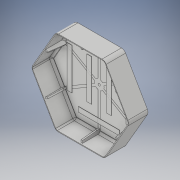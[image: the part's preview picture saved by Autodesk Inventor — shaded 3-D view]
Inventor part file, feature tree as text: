
AUTODESK INVENTOR PART (.ipt)
format: ipt  version: 2019 (Build 230136000, 136)  size: 770,560 bytes
history: native  units: mm
features: projected_geometry x23, sketch x10, extrude x5, plane x3, fillet x3, other x3, shell x1, pattern_circular x1
ambient origin geometry x8: Origin, YZ Plane, XZ Plane, XY Plane, X Axis, Y Axis, Z Axis, Center Point
bodies: Solid1 (feature_tree)
feature tree (49):
  extrude  "Extrusion1"  Depth=40.0mm TaperAngle=0.0deg
  shell  "Shell1"  Thickness=1.5mm
  extrude  "Extrusion9"  Depth=10.0mm
  plane  "Work Plane1"
  plane  "Work Plane2"
  plane  "Work Plane3"
  sketch  "Sketch12"  dims[d56=2.0mm]
  extrude  "Extrusion5"  Depth=5.0mm
  extrude  "Extrusion6"  TaperAngle=60.0deg  [1 undecoded]
  extrude  "Extrusion8"  TaperAngle=90.0deg  [1 undecoded]
  pattern_circular  "Circular Pattern1"  [2 undecoded]
  fillet  "Fillet1"  Radius=36.0mm
  fillet  "Fillet2"  Radius=60.0mm
  fillet  "Fillet4"  Radius=60.0mm
  sketch  "Sketch5"  dims[d12=1.0mm d37=5.0mm]
  sketch  "Sketch6"  dims[d44=10.0mm d45=60.0deg]
  sketch  "Sketch7"  dims[d46=90.0deg d47=90.0deg]
  other  "Work Axis4"
  other  "Work Axis5"
  other  "Work Axis6"
  sketch  "Sketch13"  dims[d57=3.0mm d58=8.0mm d59=36.0mm d60=0.0mm d70=60.0mm d72=360.0deg d74=60.0mm d75=360.0deg d77=3.0mm d78=30.0mm d79=20.0mm d80=0.0mm d138=10.0mm d139=85.0mm d140=40.0mm d142=40.5mm d143=10.0mm d145=10.0mm d147=130.0mm d149=0.5mm d150=0.0mm]
  sketch  "Sketch1"  dims[d0=175.0mm d2=40.0mm d3=0.0mm d4=1.5mm]
  sketch  "Sketch4"  dims[d10=4.0mm d11=10.0mm]
  projected_geometry  "Projected Loop3"
  sketch  "Sketch8"  dims[d52=5.5mm]
  projected_geometry  "Projected Loop4"
  sketch  "Sketch9"  dims[d53=0.01mm d54=0.0mm]
  projected_geometry  "Projected Loop5"
  sketch  "Sketch11"  dims[d55=5.0mm]
  projected_geometry  "Projected Loop6"
  projected_geometry  "Projected Loop7"
  projected_geometry  "Projected Loop8"
  projected_geometry  "Projected Loop9"
  projected_geometry  "Projected Loop10"
  projected_geometry  "Projected Loop11"
  projected_geometry  "Projected Loop12"
  projected_geometry  "Projected Loop13"
  projected_geometry  "Projected Loop14"
  projected_geometry  "Projected Loop15"
  projected_geometry  "Projected Loop16"
  projected_geometry  "Projected Loop17"
  projected_geometry  "Projected Loop18"
  projected_geometry  "Projected Loop19"
  projected_geometry  "Projected Loop20"
  projected_geometry  "Projected Loop21"
  projected_geometry  "Projected Loop22"
  projected_geometry  "Projected Loop23"
  projected_geometry  "Projected Loop24"
  projected_geometry  "Projected Loop25"
note: 4 required parameter values undecoded (feature->parameter linkage not recoverable at this tier; creation-order binding heuristic only, values carry confidence <= 0.55)
